# Revit family: Sanitary_Taps-And-Mixers_Sanindusa_New-Icone-Bath-Shower-Mixer
name_source: partatom
category: Plumbing Fixtures
revit_build: Autodesk Revit 2018 (Build: 20170223_1515(x64)
units: mm (PartAtom-declared; Revit-internal decimal feet)

## family parameters
Always vertical = Yes
Cut with Voids When Loaded = No
OmniClass Number = 23.45.00.00
OmniClass Title = Sanitary, Laundry, and Cleaning Equipment
Part Type = Normal
Room Calculation Point = No
Round Connector Dimension = Use Diameter
Shared = No
Work Plane-Based = No

## types (1)
- Sanitary_Taps-And-Mixers_Sanindusa_New-Icone-Bath-Shower-Mixer
    AssetType = Fixed
    BodyMaterial = Brass
    CartridgeType = D35 mm open ceramic cartridge
    Constituents = Single lever shower mixer with hand shower, 150cm flexible for hand shower and support for hand shower all inluded.
    Cost = 0 $
    Description = Bath|shower mixer
    Edition number = 1
    Element Type = FAUCET: A small diameter valve, with a free outlet, from which water is drawn.
    FaucetFunction = Mixed
    FaucetOperation = Other
    FaucetTopDescription = Single lever
    FaucetType = SprayMixing
    Features = Ceramic cartridge technology. Single lever mixer  with hand shower, flexible and  shower rest included.
    Finish = Chrome plated
    FittingCentres = 150 mm
    FlowCoefficient = water flow to 3 bar**: 21L/min.(spout) | 11L/min.(hand shower)
(** total opening at 50% hot water + 50% cold water)
    FlowRateMaximum = Debit (3 bar): hand-shower 11 L/min - spout 21 L/min
    InletConnectionType = 2 x M10x1-3/8 stainless steel flexible supply hoses
    Installation Instructions = https://www.tec.sanindusa.pt
    InstallationDate = 1900-12-31T23:59:59
    Manufacturer = Sanindusa
    ManufacturerName = Sanindusa
    ManufacturerURL = www.tec.sanindusa.pt
    Material = Brass
    ModelNumber = 5260801
    ModelReference = New Ícone
    Name = New ícone bath|shower mixer
    NominalHeight = 98 mm
    NominalLength = 215 mm
    NominalWidth = 172 mm
    OperatingMechanismMaterial = Brass
    Pre-defined type (IFC) = FAUCET
    Product Guid = ad4b01f2-2a41-4a09-8513-0014b1b0f4be
    Product data url = https://bimobject.com
    ProductInformation = https://www.tec.sanindusa.pt
    ProductionYear = 2018
    Size = 215x172x98
    TestPressure = 10 bar
    Type (IFC) = IfcValveType
    URL = www.tec.sanindusa.pt
    Uniclass2015Version = Products v1.6
    ValveMechanism = UNSET
    ValveOperation = UNSET
    ValvePattern = UNSET
    Version = 1
    WarrantyDescription = https://www.tec.sanindusa.pt
    WarrantyDurationParts = 5
    WarrantyDurationUnit = year
    WarrantyStartDate = 1900-12-31T23:59:59
1900-12-31T23:59:59
    Weight = 2.20 kg
    WorkingPressure = 3 bar

## geometry (parser evidence)
native form markers: Sweep x4
no freeform markers — native parametric forms only
